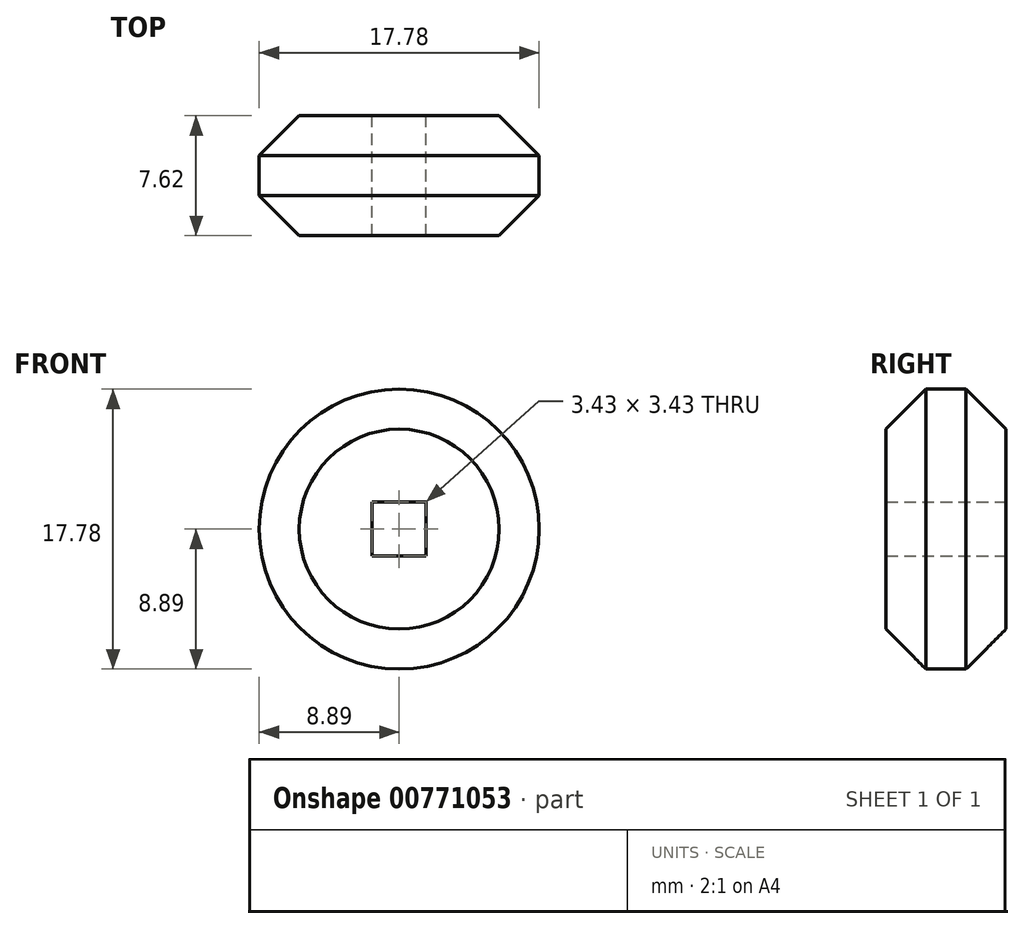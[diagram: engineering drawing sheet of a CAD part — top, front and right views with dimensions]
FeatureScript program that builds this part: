
annotation { "Feature Type Name" : "Feature", "Feature Type Description" : "" }
export const myFeature = defineFeature(function(context is Context, id is Id, definition is map)
    precondition{}
    {
        {
            var Q0;
            Q0=qCreatedBy(makeId("Front.planeOp"),FACE);
            var sketch = newSketch(context, id + "F0", { "sketchPlane" : qUnion([Q0])});
            skCircle(sketch, "E0", {"center": v(0, 0) * mm, "radius": 8.9 * mm});
            skLineSegment(sketch, "E1.bottom", {"start": v(-1.71, -1.71) * mm, "end": v(1.71, -1.71) * mm});
            skLineSegment(sketch, "E1.top", {"start": v(-1.71, 1.71) * mm, "end": v(1.71, 1.71) * mm});
            skLineSegment(sketch, "E1.right", {"start": v(1.71, -1.71) * mm, "end": v(1.71, 1.71) * mm});
            skLineSegment(sketch, "E2", {"start": v(-1.71, 1.71) * mm, "end": v(-1.71, -1.71) * mm});
            skSolve(sketch);
        }
        {
            var Q0;
            Q0=makeQuery(id+"F0.imprint","IMPRINT",FACE,{"disambiguationData":[TD([[makeQuery(id+"F0.imprint","IMPRINT",EDGE,{"derivedFrom":sQuery(id+"F0.wireOp",EDGE,"E0")}),1.0]])]});
            extrude(context, id + "F1", {"entities" : qUnion([Q0]), "depth" : 7.62 * mm, "offsetDistance" : 25.4 * mm});
        }
        {
            var Q0;
            Q0=makeQuery(id+"F1.opExtrude","CAP_EDGE",EDGE,{"disambiguationData":[OSD([sQuery(id+"F0.wireOp",EDGE,"E0")])],"isStart":true});
            var Q1;
            Q1=makeQuery(id+"F1.opExtrude","CAP_EDGE",EDGE,{"disambiguationData":[OSD([sQuery(id+"F0.wireOp",EDGE,"E0")])],"isStart":false});
            chamfer(context, id + "F2", {"entities" : qUnion([Q0, Q1]), "width" : 2.54 * mm, "tangentPropagation" : true});
        }
    });
